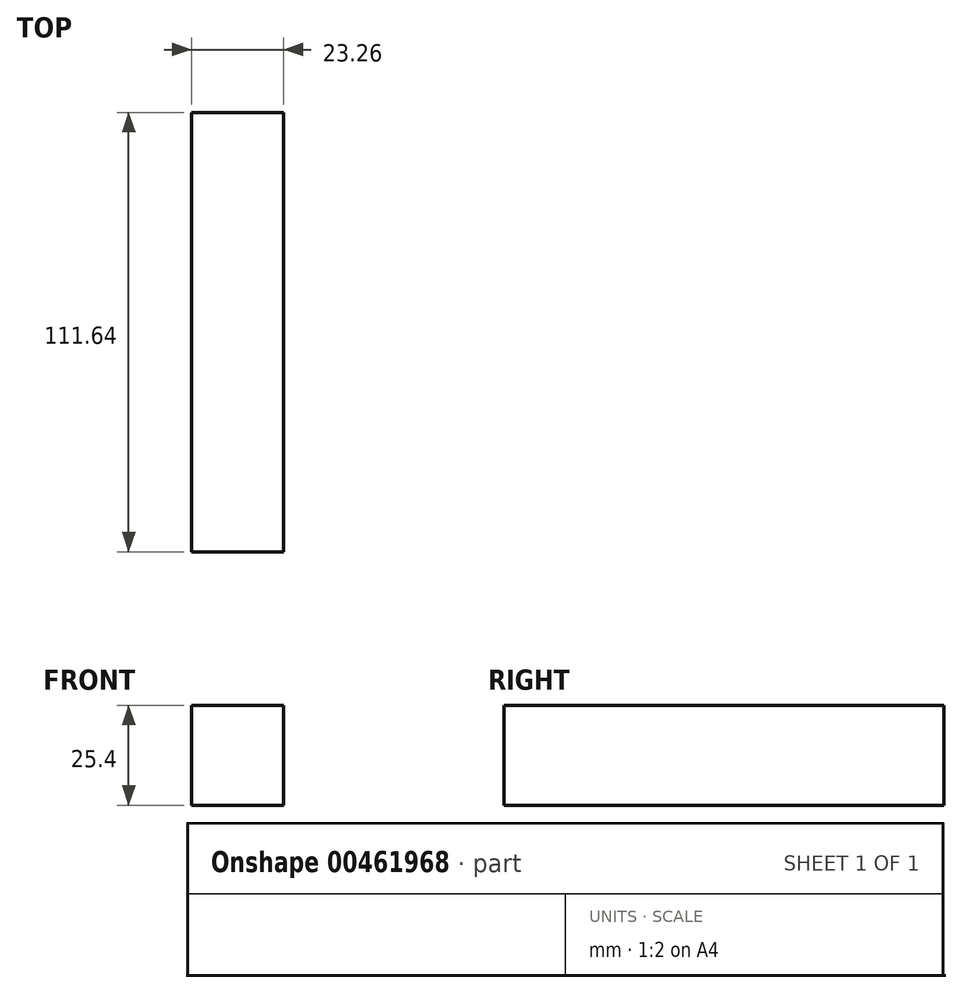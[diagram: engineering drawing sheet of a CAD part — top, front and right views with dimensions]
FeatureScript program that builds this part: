
annotation { "Feature Type Name" : "Feature", "Feature Type Description" : "" }
export const myFeature = defineFeature(function(context is Context, id is Id, definition is map)
    precondition{}
    {
        {
            var Q0;
            Q0=qCreatedBy(makeId("Top.planeOp"),FACE);
            var sketch = newSketch(context, id + "F0", { "sketchPlane" : qUnion([Q0])});
            skLineSegment(sketch, "E0.bottom", {"start": v(11.63, 55.82) * mm, "end": v(-11.63, 55.82) * mm});
            skLineSegment(sketch, "E0.top", {"start": v(11.63, -55.82) * mm, "end": v(-11.63, -55.82) * mm});
            skLineSegment(sketch, "E0.left", {"start": v(11.63, 55.82) * mm, "end": v(11.63, -55.82) * mm});
            skLineSegment(sketch, "E0.right", {"start": v(-11.63, 55.82) * mm, "end": v(-11.63, -55.82) * mm});
            skPoint(sketch, "E0.middle", {"position": v(0, 0) * mm});
            skSolve(sketch);
        }
        {
            var Q0;
            Q0=makeQuery(id+"F0.imprint","IMPRINT",FACE,{"disambiguationData":[TD([[makeQuery(id+"F0.imprint","IMPRINT",EDGE,{"derivedFrom":sQuery(id+"F0.wireOp",EDGE,"E0.bottom")}),1.0]])]});
            extrude(context, id + "F1", {"entities" : qUnion([Q0]), "depth" : 25.4 * mm});
        }
    });
